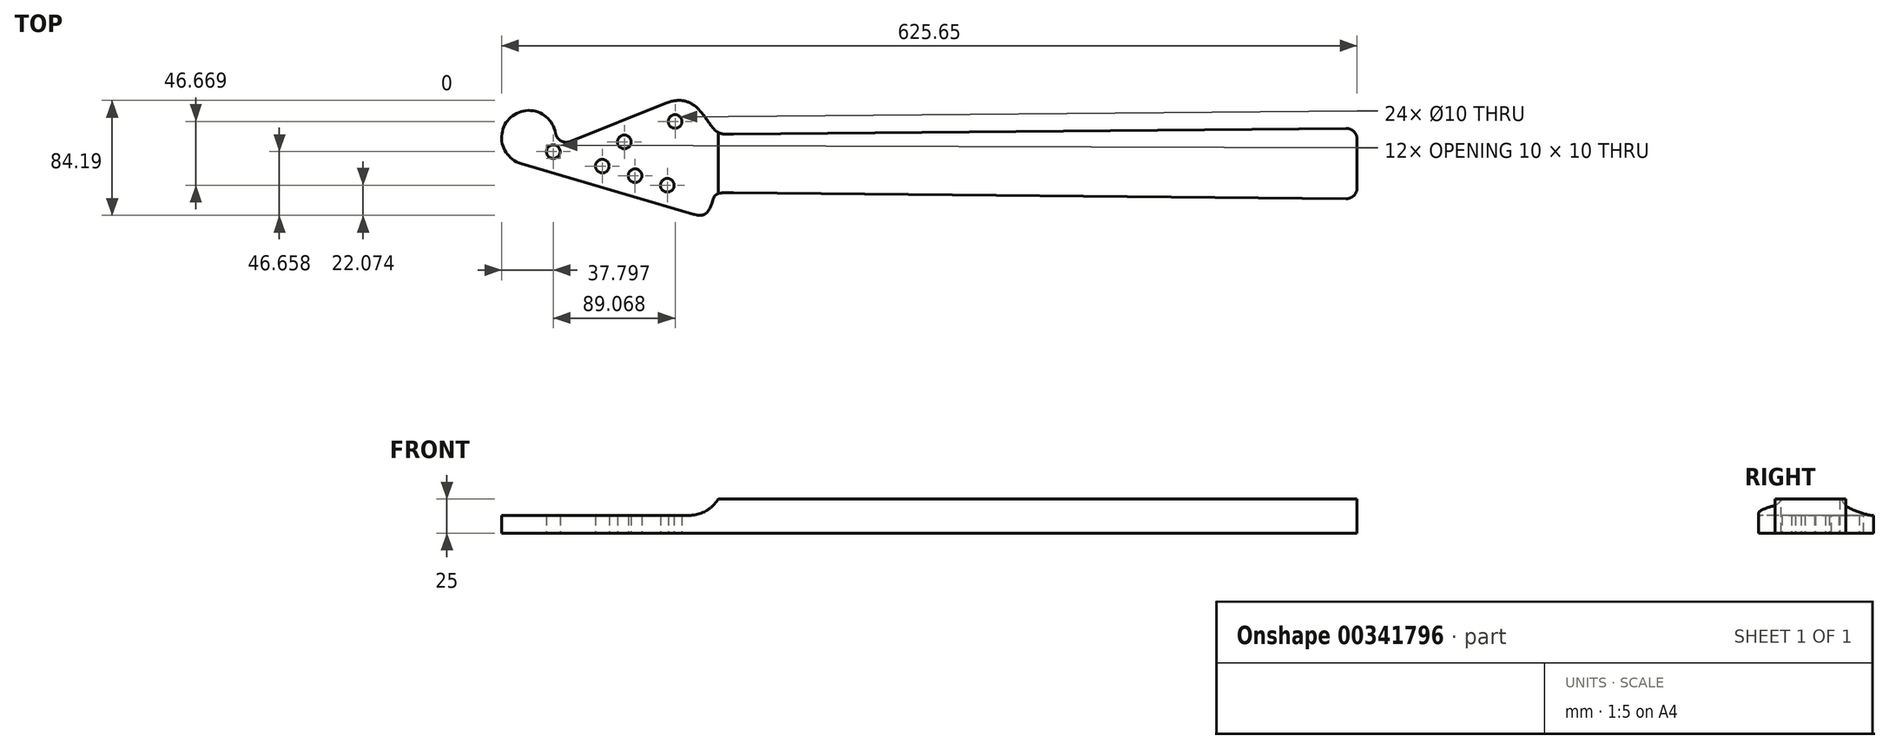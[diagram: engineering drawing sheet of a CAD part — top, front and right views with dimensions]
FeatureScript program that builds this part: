
annotation { "Feature Type Name" : "Feature", "Feature Type Description" : "" }
export const myFeature = defineFeature(function(context is Context, id is Id, definition is map)
    precondition{}
    {
        {
            var Q0;
            Q0=qCreatedBy(makeId("Top.planeOp"),FACE);
            var sketch = newSketch(context, id + "F0", { "sketchPlane" : qUnion([Q0])});
            skLineSegment(sketch, "E0", {"start": v(-545.56, 0) * mm, "end": v(270.45, 0) * mm, "construction": true});
            skLineSegment(sketch, "E1", {"start": v(-514.65, 21.5) * mm, "end": v(-514.65, -21.5) * mm, "construction": true});
            skText(sketch, "E2", { "text": "Nut", "fontName": "OpenSans-Regular.ttf"});
            skLineSegment(sketch, "E3", {"start": v(120.35, 27.5) * mm, "end": v(120.35, -27.5) * mm, "construction": true});
            skText(sketch, "E4", { "text": "Bridge\n", "fontName": "OpenSans-Regular.ttf"});
            skLineSegment(sketch, "E5", {"start": v(-514.65, 21.5) * mm, "end": v(120.35, 27.5) * mm, "construction": true});
            skLineSegment(sketch, "E6", {"start": v(-514.65, -21.5) * mm, "end": v(120.35, -27.5) * mm, "construction": true});
            skLineSegment(sketch, "E7", {"start": v(-514.65, 0) * mm, "end": v(120.35, 0) * mm});
            const initialGuessF0  = {"E2": [-0.53875, 0.11756, 1, 0, 0.01067], "E4": [0.1311, 0.11455, 1, 0, 0.02259]};
            skSetInitialGuess(sketch, initialGuessF0);
            skSolve(sketch);
        }
        {
            var Q0;
            Q0=qCreatedBy(makeId("Top.planeOp"),FACE);
            var sketch = newSketch(context, id + "F1", { "sketchPlane" : qUnion([Q0])});
            skLineSegment(sketch, "E8", {"start": v(-514.65, 21.5) * mm, "end": v(-514.65, -21.5) * mm});
            skSolve(sketch);
        }
        {
            var Q0;
            Q0=qCreatedBy(makeId("Top.planeOp"),FACE);
            var sketch = newSketch(context, id + "F2", { "sketchPlane" : qUnion([Q0])});
            skLineSegment(sketch, "E9", {"start": v(-479, 35.64) * mm, "end": v(-479, 0) * mm});
            skLineSegment(sketch, "E10", {"start": v(-514.65, 37.76) * mm, "end": v(120.35, 0) * mm, "construction": true});
            skLineSegment(sketch, "E11", {"start": v(120.35, 0) * mm, "end": v(-514.65, -21.5) * mm, "construction": true});
            skLineSegment(sketch, "E12", {"start": v(-514.65, 0) * mm, "end": v(-514.65, 37.76) * mm});
            skLineSegment(sketch, "E13", {"start": v(-514.65, 0) * mm, "end": v(-479, 0) * mm});
            skLineSegment(sketch, "E14", {"start": v(-445.37, 33.64) * mm, "end": v(-445.37, 0) * mm});
            skLineSegment(sketch, "E15", {"start": v(-445.37, 0) * mm, "end": v(-479, 0) * mm});
            skLineSegment(sketch, "E16", {"start": v(-445.37, 0) * mm, "end": v(-413.62, 0) * mm});
            skLineSegment(sketch, "E17", {"start": v(-413.62, 0) * mm, "end": v(-413.62, 31.75) * mm});
            skLineSegment(sketch, "E18", {"start": v(-413.62, 0) * mm, "end": v(-383.65, 0) * mm});
            skLineSegment(sketch, "E19", {"start": v(-383.65, 0) * mm, "end": v(-383.65, 29.97) * mm});
            skLineSegment(sketch, "E20", {"start": v(-383.65, 0) * mm, "end": v(-355.36, 0) * mm});
            skLineSegment(sketch, "E21", {"start": v(-355.36, 0) * mm, "end": v(-355.36, 28.29) * mm});
            skLineSegment(sketch, "E22", {"start": v(-355.36, 0) * mm, "end": v(-328.66, 0) * mm});
            skLineSegment(sketch, "E23", {"start": v(-328.66, 0) * mm, "end": v(-328.66, 26.7) * mm});
            skLineSegment(sketch, "E24", {"start": v(-328.66, 0) * mm, "end": v(-303.46, 0) * mm});
            skLineSegment(sketch, "E25", {"start": v(-303.46, 0) * mm, "end": v(-303.46, 25.2) * mm});
            skLineSegment(sketch, "E26", {"start": v(-303.46, 0) * mm, "end": v(-279.67, 0) * mm});
            skLineSegment(sketch, "E27", {"start": v(-279.67, 0) * mm, "end": v(-279.67, 23.79) * mm});
            skLineSegment(sketch, "E28", {"start": v(-279.67, 0) * mm, "end": v(-257.22, 0) * mm});
            skLineSegment(sketch, "E29", {"start": v(-257.22, 0) * mm, "end": v(-257.22, 22.45) * mm});
            skLineSegment(sketch, "E30", {"start": v(-257.22, 0) * mm, "end": v(-236.03, 0) * mm});
            skLineSegment(sketch, "E31", {"start": v(-236.03, 0) * mm, "end": v(-236.03, 21.2) * mm});
            skLineSegment(sketch, "E32", {"start": v(-236.03, 0) * mm, "end": v(-216.03, 0) * mm});
            skPoint(sketch, "E32.endSnap0", {"position": v(-246.63, 0) * mm});
            skLineSegment(sketch, "E33", {"start": v(-216.03, 0) * mm, "end": v(-216.03, 20) * mm});
            skLineSegment(sketch, "E34", {"start": v(-216.03, 0) * mm, "end": v(-197.15, 0) * mm});
            skLineSegment(sketch, "E35", {"start": v(-197.15, 0) * mm, "end": v(-197.15, 18.88) * mm});
            skLineSegment(sketch, "E36", {"start": v(-197.15, 0) * mm, "end": v(-179.33, 0) * mm});
            skLineSegment(sketch, "E37", {"start": v(-179.33, 0) * mm, "end": v(-179.33, 17.82) * mm});
            skLineSegment(sketch, "E38", {"start": v(-179.33, 0) * mm, "end": v(-162.5, 0) * mm});
            skLineSegment(sketch, "E39", {"start": v(-162.5, 0) * mm, "end": v(-162.5, 16.82) * mm});
            skLineSegment(sketch, "E40", {"start": v(-162.5, 0) * mm, "end": v(-146.63, 0) * mm});
            skLineSegment(sketch, "E41", {"start": v(-146.63, 0) * mm, "end": v(-146.63, 15.88) * mm});
            skLineSegment(sketch, "E42", {"start": v(-146.63, 0) * mm, "end": v(-131.65, 0) * mm});
            skLineSegment(sketch, "E43", {"start": v(-131.65, 0) * mm, "end": v(-131.65, 14.98) * mm});
            skLineSegment(sketch, "E44", {"start": v(-131.65, 0) * mm, "end": v(-117.5, 0) * mm});
            skLineSegment(sketch, "E45", {"start": v(-117.5, 0) * mm, "end": v(-117.5, 14.14) * mm});
            skLineSegment(sketch, "E46", {"start": v(-117.5, 0) * mm, "end": v(-104.16, 0) * mm});
            skLineSegment(sketch, "E47", {"start": v(-104.16, 0) * mm, "end": v(-104.16, 13.35) * mm});
            skLineSegment(sketch, "E48", {"start": v(-104.16, 0) * mm, "end": v(-91.56, 0) * mm});
            skLineSegment(sketch, "E49", {"start": v(-91.56, 0) * mm, "end": v(-91.56, 12.6) * mm});
            skLineSegment(sketch, "E50", {"start": v(-91.56, 0) * mm, "end": v(-79.66, 0) * mm});
            skLineSegment(sketch, "E51", {"start": v(-79.66, 0) * mm, "end": v(-79.66, 11.9) * mm});
            skLineSegment(sketch, "E52", {"start": v(-79.66, 0) * mm, "end": v(-68.44, 0) * mm});
            skLineSegment(sketch, "E53", {"start": v(-68.44, 0) * mm, "end": v(-68.44, 11.23) * mm});
            skSolve(sketch);
        }
        {
            var Q0;
            Q0=qCreatedBy(makeId("Top.planeOp"),FACE);
            var sketch = newSketch(context, id + "F3", { "sketchPlane" : qUnion([Q0])});
            skLineSegment(sketch, "E54", {"start": v(-514.65, 21.5) * mm, "end": v(-514.65, -21.5) * mm});
            skLineSegment(sketch, "E55", {"start": v(-514.65, -21.5) * mm, "end": v(-66.51, -25.73) * mm});
            skLineSegment(sketch, "E56", {"start": v(-58.44, -17.73) * mm, "end": v(-58.44, 17.73) * mm});
            skLineSegment(sketch, "E57", {"start": v(-66.51, 25.73) * mm, "end": v(-514.65, 21.5) * mm});
            skLineSegment(sketch, "E58", {"start": v(-68.44, 0) * mm, "end": v(-58.44, 0) * mm});
            skPoint(sketch, "E59.visualSharp", {"position": v(-58.44, -25.81) * mm});
            skArc(sketch, "E59.filletArc", {"start": v(-66.51, -25.73) * mm, "mid": v(-60.8, -23.42) * mm, "end": v(-58.44, -17.73) * mm});
            skPoint(sketch, "E60.visualSharp", {"position": v(-58.44, 25.81) * mm});
            skArc(sketch, "E60.filletArc", {"start": v(-58.44, 17.73) * mm, "mid": v(-60.8, 23.42) * mm, "end": v(-66.51, 25.73) * mm});
            skSolve(sketch);
        }
        {
            var Q0;
            Q0=qSketchRegion(id+"F3",true);
            extrude(context, id + "F4", {"entities" : qUnion([Q0]), "depth" : 6 * mm});
        }
        {
            var Q0;
            Q0=makeQuery(id+"F4.opExtrude","CAP_FACE",FACE,{"disambiguationData":[OSD([sQuery(id+"F3.wireOp",EDGE,"E54"),sQuery(id+"F3.wireOp",EDGE,"E55"),sQuery(id+"F3.wireOp",EDGE,"E56"),sQuery(id+"F3.wireOp",EDGE,"E57")])],"isStart":false});
            cPlane(context, id + "F5", {"entities" : qUnion([Q0]), "cplaneType" : CPlaneType.OFFSET, "offset" : 0 * mm, "width" : 150 * mm, "height" : 150 * mm});
        }
        {
            var Q0;
            Q0=qCreatedBy(id+"F5.planeOp",FACE);
            var sketch = newSketch(context, id + "F6", { "sketchPlane" : qUnion([Q0])});
            skCircle(sketch, "E61", {"center": v(-429.5, 0) * mm, "radius": 3 * mm});
            skCircle(sketch, "E62", {"center": v(-369.5, 0) * mm, "radius": 3 * mm});
            skCircle(sketch, "E63", {"center": v(-316.06, 0) * mm, "radius": 3 * mm});
            skCircle(sketch, "E64", {"center": v(-268.45, 0) * mm, "radius": 3 * mm});
            skCircle(sketch, "E65", {"center": v(-226.03, 12.11) * mm, "radius": 3 * mm});
            skCircle(sketch, "E66", {"center": v(-226.03, -12.11) * mm, "radius": 3 * mm});
            skLineSegment(sketch, "E67", {"start": v(-226.03, 0) * mm, "end": v(-226.03, 12.11) * mm, "construction": true});
            skCircle(sketch, "E68", {"center": v(-170.92, 0) * mm, "radius": 3 * mm});
            skCircle(sketch, "E69", {"center": v(-139.14, 0) * mm, "radius": 3 * mm});
            skCircle(sketch, "E70", {"center": v(-110.83, 0) * mm, "radius": 3 * mm});
            skCircle(sketch, "E71", {"center": v(-85.6, 0) * mm, "radius": 3 * mm});
            skLineSegment(sketch, "E72.0", {"start": v(-514.65, 21.5) * mm, "end": v(120.35, 27.5) * mm});
            skLineSegment(sketch, "E73", {"start": v(-226.03, 0) * mm, "end": v(-226.03, 24.23) * mm, "construction": true});
            skSolve(sketch);
        }
        {
            var Q0;
            Q0=qSketchRegion(id+"F6",true);
            var Q1;
            Q1=makeQuery(id+"F4.opExtrude","CAP_FACE",FACE,{"disambiguationData":[OSD([sQuery(id+"F3.wireOp",EDGE,"E54"),sQuery(id+"F3.wireOp",EDGE,"E55"),sQuery(id+"F3.wireOp",EDGE,"E56"),sQuery(id+"F3.wireOp",EDGE,"E57")])],"isStart":true});
            extrude(context, id + "F7", {"entities" : qUnion([Q0]), "operationType" : NewBodyOperationType.REMOVE, "oppositeDirection" : true, "endBoundEntityFace" : qUnion([Q1]), "depth" : 2 * mm});
        }
        {
            var Q0;
            Q0=makeQuery(id+"F4.opExtrude","SWEPT_FACE",FACE,{"disambiguationData":[OSD([sQuery(id+"F3.wireOp",EDGE,"E56")])]});
            var sketch = newSketch(context, id + "F8", { "sketchPlane" : qUnion([Q0])});
            skArc(sketch, "E74", {"start": v(53.48, 0) * mm, "mid": v(0, 6) * mm, "end": v(-53.48, 0) * mm});
            skLineSegment(sketch, "E75", {"start": v(-53.48, 0) * mm, "end": v(-53.48, 6) * mm});
            skLineSegment(sketch, "E76", {"start": v(-53.48, 6) * mm, "end": v(53.48, 6) * mm});
            skLineSegment(sketch, "E77", {"start": v(53.48, 6) * mm, "end": v(53.48, 0) * mm});
            skSolve(sketch);
        }
        {
            var Q0;
            Q0=qSketchRegion(id+"F8",true);
            extrude(context, id + "F9", {"entities" : qUnion([Q0]), "operationType" : NewBodyOperationType.REMOVE, "endBound" : BoundingType.THROUGH_ALL, "oppositeDirection" : true, "depth" : 25 * mm});
        }
        {
            var Q0;
            Q0=qCreatedBy(id+"F5.planeOp",FACE);
            var sketch = newSketch(context, id + "F10", { "sketchPlane" : qUnion([Q0])});
            skLineSegment(sketch, "E78.0", {"start": v(-514.65, 21.5) * mm, "end": v(-514.65, -21.5) * mm});
            skLineSegment(sketch, "E79.0", {"start": v(-58.44, 25.76) * mm, "end": v(-58.44, -25.76) * mm});
            skLineSegment(sketch, "E80", {"start": v(-514.65, 18.5) * mm, "end": v(-58.44, 22.81) * mm, "construction": true});
            skLineSegment(sketch, "E81", {"start": v(-514.65, -18.5) * mm, "end": v(-58.44, -22.81) * mm, "construction": true});
            skLineSegment(sketch, "E82", {"start": v(-479, 18.84) * mm, "end": v(-479, -18.84) * mm});
            skLineSegment(sketch, "E83", {"start": v(-445.37, 19.15) * mm, "end": v(-445.37, -19.15) * mm});
            skArc(sketch, "E84.0.startCap", {"start": v(-479.3, 18.84) * mm, "mid": v(-479, 19.14) * mm, "end": v(-478.7, 18.84) * mm});
            skArc(sketch, "E84.0.endCap", {"start": v(-478.7, -18.84) * mm, "mid": v(-479, -19.14) * mm, "end": v(-479.3, -18.84) * mm});
            skLineSegment(sketch, "E84.0.left", {"start": v(-478.7, 18.84) * mm, "end": v(-478.7, -18.84) * mm});
            skLineSegment(sketch, "E84.0.right", {"start": v(-479.3, 18.84) * mm, "end": v(-479.3, -18.84) * mm});
            skArc(sketch, "E85.0.startCap", {"start": v(-445.67, 19.15) * mm, "mid": v(-445.37, 19.45) * mm, "end": v(-445.07, 19.15) * mm});
            skArc(sketch, "E85.0.endCap", {"start": v(-445.07, -19.15) * mm, "mid": v(-445.37, -19.45) * mm, "end": v(-445.67, -19.15) * mm});
            skLineSegment(sketch, "E85.0.left", {"start": v(-445.07, 19.15) * mm, "end": v(-445.07, -19.15) * mm});
            skLineSegment(sketch, "E85.0.right", {"start": v(-445.67, 19.15) * mm, "end": v(-445.67, -19.15) * mm});
            skLineSegment(sketch, "E86", {"start": v(-413.62, 19.45) * mm, "end": v(-413.62, -19.45) * mm});
            skLineSegment(sketch, "E87", {"start": v(-383.65, 19.74) * mm, "end": v(-383.65, -19.74) * mm});
            skArc(sketch, "E88.0.startCap", {"start": v(-413.92, 19.45) * mm, "mid": v(-413.62, 19.75) * mm, "end": v(-413.32, 19.45) * mm});
            skArc(sketch, "E88.0.endCap", {"start": v(-413.32, -19.45) * mm, "mid": v(-413.62, -19.75) * mm, "end": v(-413.92, -19.45) * mm});
            skLineSegment(sketch, "E88.0.left", {"start": v(-413.32, 19.45) * mm, "end": v(-413.32, -19.45) * mm});
            skLineSegment(sketch, "E88.0.right", {"start": v(-413.92, 19.45) * mm, "end": v(-413.92, -19.45) * mm});
            skArc(sketch, "E89.0.startCap", {"start": v(-383.95, 19.74) * mm, "mid": v(-383.65, 20.04) * mm, "end": v(-383.35, 19.74) * mm});
            skArc(sketch, "E89.0.endCap", {"start": v(-383.35, -19.74) * mm, "mid": v(-383.65, -20.04) * mm, "end": v(-383.95, -19.74) * mm});
            skLineSegment(sketch, "E89.0.left", {"start": v(-383.35, 19.74) * mm, "end": v(-383.35, -19.74) * mm});
            skLineSegment(sketch, "E89.0.right", {"start": v(-383.95, 19.74) * mm, "end": v(-383.95, -19.74) * mm});
            skLineSegment(sketch, "E90", {"start": v(-355.36, -20) * mm, "end": v(-355.36, 20) * mm});
            skArc(sketch, "E91.0.startCap", {"start": v(-355.06, -20) * mm, "mid": v(-355.36, -20.3) * mm, "end": v(-355.66, -20) * mm});
            skArc(sketch, "E91.0.endCap", {"start": v(-355.66, 20) * mm, "mid": v(-355.36, 20.3) * mm, "end": v(-355.06, 20) * mm});
            skLineSegment(sketch, "E91.0.left", {"start": v(-355.66, -20) * mm, "end": v(-355.66, 20) * mm});
            skLineSegment(sketch, "E91.0.right", {"start": v(-355.06, -20) * mm, "end": v(-355.06, 20) * mm});
            skLineSegment(sketch, "E92", {"start": v(-328.66, -20.26) * mm, "end": v(-328.66, 20.26) * mm});
            skArc(sketch, "E93.0.startCap", {"start": v(-328.36, -20.26) * mm, "mid": v(-328.66, -20.56) * mm, "end": v(-328.96, -20.26) * mm});
            skArc(sketch, "E93.0.endCap", {"start": v(-328.96, 20.26) * mm, "mid": v(-328.66, 20.56) * mm, "end": v(-328.36, 20.26) * mm});
            skLineSegment(sketch, "E93.0.left", {"start": v(-328.96, -20.26) * mm, "end": v(-328.96, 20.26) * mm});
            skLineSegment(sketch, "E93.0.right", {"start": v(-328.36, -20.26) * mm, "end": v(-328.36, 20.26) * mm});
            skLineSegment(sketch, "E94", {"start": v(-303.46, 20.5) * mm, "end": v(-303.46, -20.5) * mm});
            skArc(sketch, "E95.0.startCap", {"start": v(-303.76, 20.5) * mm, "mid": v(-303.46, 20.8) * mm, "end": v(-303.16, 20.5) * mm});
            skArc(sketch, "E95.0.endCap", {"start": v(-303.16, -20.5) * mm, "mid": v(-303.46, -20.8) * mm, "end": v(-303.76, -20.5) * mm});
            skLineSegment(sketch, "E95.0.left", {"start": v(-303.16, 20.5) * mm, "end": v(-303.16, -20.5) * mm});
            skLineSegment(sketch, "E95.0.right", {"start": v(-303.76, 20.5) * mm, "end": v(-303.76, -20.5) * mm});
            skLineSegment(sketch, "E96", {"start": v(-279.67, 20.72) * mm, "end": v(-279.67, -20.72) * mm});
            skArc(sketch, "E97.0.startCap", {"start": v(-279.97, 20.72) * mm, "mid": v(-279.67, 21.02) * mm, "end": v(-279.37, 20.72) * mm});
            skArc(sketch, "E97.0.endCap", {"start": v(-279.37, -20.72) * mm, "mid": v(-279.67, -21.02) * mm, "end": v(-279.97, -20.72) * mm});
            skLineSegment(sketch, "E97.0.left", {"start": v(-279.37, 20.72) * mm, "end": v(-279.37, -20.72) * mm});
            skLineSegment(sketch, "E97.0.right", {"start": v(-279.97, 20.72) * mm, "end": v(-279.97, -20.72) * mm});
            skLineSegment(sketch, "E98", {"start": v(-257.22, -20.93) * mm, "end": v(-257.22, 20.93) * mm});
            skArc(sketch, "E99.0.startCap", {"start": v(-256.92, -20.93) * mm, "mid": v(-257.22, -21.23) * mm, "end": v(-257.52, -20.93) * mm});
            skArc(sketch, "E99.0.endCap", {"start": v(-257.52, 20.93) * mm, "mid": v(-257.22, 21.23) * mm, "end": v(-256.92, 20.93) * mm});
            skLineSegment(sketch, "E99.0.left", {"start": v(-257.52, -20.93) * mm, "end": v(-257.52, 20.93) * mm});
            skLineSegment(sketch, "E99.0.right", {"start": v(-256.92, -20.93) * mm, "end": v(-256.92, 20.93) * mm});
            skLineSegment(sketch, "E100", {"start": v(-236.03, 21.13) * mm, "end": v(-236.03, -21.13) * mm});
            skArc(sketch, "E101.0.startCap", {"start": v(-236.33, 21.13) * mm, "mid": v(-236.03, 21.43) * mm, "end": v(-235.73, 21.13) * mm});
            skArc(sketch, "E101.0.endCap", {"start": v(-235.73, -21.13) * mm, "mid": v(-236.03, -21.43) * mm, "end": v(-236.33, -21.13) * mm});
            skLineSegment(sketch, "E101.0.left", {"start": v(-235.73, 21.13) * mm, "end": v(-235.73, -21.13) * mm});
            skLineSegment(sketch, "E101.0.right", {"start": v(-236.33, 21.13) * mm, "end": v(-236.33, -21.13) * mm});
            skLineSegment(sketch, "E102", {"start": v(-216.03, 21.32) * mm, "end": v(-216.03, -21.32) * mm});
            skArc(sketch, "E103.0.startCap", {"start": v(-216.33, 21.32) * mm, "mid": v(-216.03, 21.62) * mm, "end": v(-215.73, 21.32) * mm});
            skArc(sketch, "E103.0.endCap", {"start": v(-215.73, -21.32) * mm, "mid": v(-216.03, -21.62) * mm, "end": v(-216.33, -21.32) * mm});
            skLineSegment(sketch, "E103.0.left", {"start": v(-215.73, 21.32) * mm, "end": v(-215.73, -21.32) * mm});
            skLineSegment(sketch, "E103.0.right", {"start": v(-216.33, 21.32) * mm, "end": v(-216.33, -21.32) * mm});
            skLineSegment(sketch, "E104", {"start": v(-197.15, 21.5) * mm, "end": v(-197.15, -21.5) * mm});
            skArc(sketch, "E105.0.startCap", {"start": v(-197.45, 21.5) * mm, "mid": v(-197.15, 21.8) * mm, "end": v(-196.85, 21.5) * mm});
            skArc(sketch, "E105.0.endCap", {"start": v(-196.85, -21.5) * mm, "mid": v(-197.15, -21.8) * mm, "end": v(-197.45, -21.5) * mm});
            skLineSegment(sketch, "E105.0.left", {"start": v(-196.85, 21.5) * mm, "end": v(-196.85, -21.5) * mm});
            skLineSegment(sketch, "E105.0.right", {"start": v(-197.45, 21.5) * mm, "end": v(-197.45, -21.5) * mm});
            skLineSegment(sketch, "E106", {"start": v(-179.33, 21.67) * mm, "end": v(-179.33, -21.67) * mm});
            skArc(sketch, "E107.0.startCap", {"start": v(-179.63, 21.67) * mm, "mid": v(-179.33, 21.97) * mm, "end": v(-179.03, 21.67) * mm});
            skArc(sketch, "E107.0.endCap", {"start": v(-179.03, -21.67) * mm, "mid": v(-179.33, -21.97) * mm, "end": v(-179.63, -21.67) * mm});
            skLineSegment(sketch, "E107.0.left", {"start": v(-179.03, 21.67) * mm, "end": v(-179.03, -21.67) * mm});
            skLineSegment(sketch, "E107.0.right", {"start": v(-179.63, 21.67) * mm, "end": v(-179.63, -21.67) * mm});
            skLineSegment(sketch, "E108", {"start": v(-162.5, 21.83) * mm, "end": v(-162.5, -21.83) * mm});
            skArc(sketch, "E109.0.startCap", {"start": v(-162.8, 21.83) * mm, "mid": v(-162.5, 22.13) * mm, "end": v(-162.2, 21.83) * mm});
            skArc(sketch, "E109.0.endCap", {"start": v(-162.2, -21.83) * mm, "mid": v(-162.5, -22.13) * mm, "end": v(-162.8, -21.83) * mm});
            skLineSegment(sketch, "E109.0.left", {"start": v(-162.2, 21.83) * mm, "end": v(-162.2, -21.83) * mm});
            skLineSegment(sketch, "E109.0.right", {"start": v(-162.8, 21.83) * mm, "end": v(-162.8, -21.83) * mm});
            skLineSegment(sketch, "E110", {"start": v(-146.63, 21.98) * mm, "end": v(-146.63, -21.98) * mm});
            skArc(sketch, "E111.0.startCap", {"start": v(-146.93, 21.98) * mm, "mid": v(-146.63, 22.28) * mm, "end": v(-146.33, 21.98) * mm});
            skArc(sketch, "E111.0.endCap", {"start": v(-146.33, -21.98) * mm, "mid": v(-146.63, -22.28) * mm, "end": v(-146.93, -21.98) * mm});
            skLineSegment(sketch, "E111.0.left", {"start": v(-146.33, 21.98) * mm, "end": v(-146.33, -21.98) * mm});
            skLineSegment(sketch, "E111.0.right", {"start": v(-146.93, 21.98) * mm, "end": v(-146.93, -21.98) * mm});
            skLineSegment(sketch, "E112", {"start": v(-131.65, 22.12) * mm, "end": v(-131.65, -22.12) * mm});
            skArc(sketch, "E113.0.startCap", {"start": v(-131.95, 22.12) * mm, "mid": v(-131.65, 22.42) * mm, "end": v(-131.35, 22.12) * mm});
            skArc(sketch, "E113.0.endCap", {"start": v(-131.35, -22.12) * mm, "mid": v(-131.65, -22.42) * mm, "end": v(-131.95, -22.12) * mm});
            skLineSegment(sketch, "E113.0.left", {"start": v(-131.35, 22.12) * mm, "end": v(-131.35, -22.12) * mm});
            skLineSegment(sketch, "E113.0.right", {"start": v(-131.95, 22.12) * mm, "end": v(-131.95, -22.12) * mm});
            skLineSegment(sketch, "E114", {"start": v(-117.5, 22.25) * mm, "end": v(-117.5, -22.25) * mm});
            skArc(sketch, "E115.0.startCap", {"start": v(-117.8, 22.25) * mm, "mid": v(-117.5, 22.55) * mm, "end": v(-117.2, 22.25) * mm});
            skArc(sketch, "E115.0.endCap", {"start": v(-117.2, -22.25) * mm, "mid": v(-117.5, -22.55) * mm, "end": v(-117.8, -22.25) * mm});
            skLineSegment(sketch, "E115.0.left", {"start": v(-117.2, 22.25) * mm, "end": v(-117.2, -22.25) * mm});
            skLineSegment(sketch, "E115.0.right", {"start": v(-117.8, 22.25) * mm, "end": v(-117.8, -22.25) * mm});
            skLineSegment(sketch, "E116", {"start": v(-104.16, 22.38) * mm, "end": v(-104.16, -22.38) * mm});
            skArc(sketch, "E117.0.startCap", {"start": v(-104.46, 22.38) * mm, "mid": v(-104.16, 22.68) * mm, "end": v(-103.86, 22.38) * mm});
            skArc(sketch, "E117.0.endCap", {"start": v(-103.86, -22.38) * mm, "mid": v(-104.16, -22.68) * mm, "end": v(-104.46, -22.38) * mm});
            skLineSegment(sketch, "E117.0.left", {"start": v(-103.86, 22.38) * mm, "end": v(-103.86, -22.38) * mm});
            skLineSegment(sketch, "E117.0.right", {"start": v(-104.46, 22.38) * mm, "end": v(-104.46, -22.38) * mm});
            skLineSegment(sketch, "E118", {"start": v(-91.56, 22.5) * mm, "end": v(-91.56, -22.5) * mm});
            skArc(sketch, "E119.0.startCap", {"start": v(-91.86, 22.5) * mm, "mid": v(-91.56, 22.8) * mm, "end": v(-91.26, 22.5) * mm});
            skArc(sketch, "E119.0.endCap", {"start": v(-91.26, -22.5) * mm, "mid": v(-91.56, -22.8) * mm, "end": v(-91.86, -22.5) * mm});
            skLineSegment(sketch, "E119.0.left", {"start": v(-91.26, 22.5) * mm, "end": v(-91.26, -22.5) * mm});
            skLineSegment(sketch, "E119.0.right", {"start": v(-91.86, 22.5) * mm, "end": v(-91.86, -22.5) * mm});
            skLineSegment(sketch, "E120", {"start": v(-79.66, -22.61) * mm, "end": v(-79.66, 22.61) * mm});
            skArc(sketch, "E121.0.startCap", {"start": v(-79.36, -22.61) * mm, "mid": v(-79.66, -22.91) * mm, "end": v(-79.96, -22.61) * mm});
            skArc(sketch, "E121.0.endCap", {"start": v(-79.96, 22.61) * mm, "mid": v(-79.66, 22.91) * mm, "end": v(-79.36, 22.61) * mm});
            skLineSegment(sketch, "E121.0.left", {"start": v(-79.96, -22.61) * mm, "end": v(-79.96, 22.61) * mm});
            skLineSegment(sketch, "E121.0.right", {"start": v(-79.36, -22.61) * mm, "end": v(-79.36, 22.61) * mm});
            skLineSegment(sketch, "E122", {"start": v(-68.44, 22.72) * mm, "end": v(-68.44, -22.72) * mm});
            skArc(sketch, "E123.0.startCap", {"start": v(-68.74, 22.72) * mm, "mid": v(-68.44, 23.02) * mm, "end": v(-68.14, 22.72) * mm});
            skArc(sketch, "E123.0.endCap", {"start": v(-68.14, -22.72) * mm, "mid": v(-68.44, -23.02) * mm, "end": v(-68.74, -22.72) * mm});
            skLineSegment(sketch, "E123.0.left", {"start": v(-68.14, 22.72) * mm, "end": v(-68.14, -22.72) * mm});
            skLineSegment(sketch, "E123.0.right", {"start": v(-68.74, 22.72) * mm, "end": v(-68.74, -22.72) * mm});
            skSolve(sketch);
        }
        {
            var Q0;
            Q0=qSketchRegion(id+"F10",true);
            extrude(context, id + "F11", {"entities" : qUnion([Q0]), "operationType" : NewBodyOperationType.REMOVE, "oppositeDirection" : true, "depth" : 4 * mm});
        }
        {
            var Q0;
            Q0=makeQuery(id+"F4.opExtrude","SWEPT_FACE",FACE,{"disambiguationData":[OSD([sQuery(id+"F3.wireOp",EDGE,"E55")])]});
            var sketch = newSketch(context, id + "F12", { "sketchPlane" : qUnion([Q0])});
            skPoint(sketch, "E124.0", {"position": v(-429.48, 6) * mm});
            skLineSegment(sketch, "E125", {"start": v(-429.48, 6) * mm, "end": v(-429.48, 0) * mm, "construction": true});
            skCircle(sketch, "E126", {"center": v(-429.48, 2) * mm, "radius": 1 * mm});
            skLineSegment(sketch, "E127", {"start": v(-298.57, 2) * mm, "end": v(-514.42, 2) * mm, "construction": true});
            skPoint(sketch, "E128.0", {"position": v(-369.49, 6) * mm});
            skLineSegment(sketch, "E129", {"start": v(-369.49, 6) * mm, "end": v(-369.49, 0) * mm, "construction": true});
            skCircle(sketch, "E130", {"center": v(-369.49, 2) * mm, "radius": 1 * mm});
            skPoint(sketch, "E131.0", {"position": v(-316.05, 6) * mm});
            skPoint(sketch, "E132.0", {"position": v(-268.44, 6) * mm});
            skPoint(sketch, "E133.0", {"position": v(-225.9, 6) * mm});
            skPoint(sketch, "E134.0", {"position": v(-170.91, 6) * mm});
            skPoint(sketch, "E135.0", {"position": v(-139.14, 6) * mm});
            skPoint(sketch, "E136.0", {"position": v(-110.83, 6) * mm});
            skPoint(sketch, "E137.0", {"position": v(-85.6, 6) * mm});
            skLineSegment(sketch, "E138", {"start": v(-85.6, 6) * mm, "end": v(-85.6, 0) * mm, "construction": true});
            skLineSegment(sketch, "E139", {"start": v(-110.83, 6) * mm, "end": v(-110.83, 0) * mm, "construction": true});
            skLineSegment(sketch, "E140", {"start": v(-139.14, 6) * mm, "end": v(-139.14, 0) * mm, "construction": true});
            skLineSegment(sketch, "E141", {"start": v(-170.91, 6) * mm, "end": v(-170.91, 0) * mm, "construction": true});
            skLineSegment(sketch, "E142", {"start": v(-225.9, 6) * mm, "end": v(-225.9, 0) * mm, "construction": true});
            skLineSegment(sketch, "E143", {"start": v(-268.44, 6) * mm, "end": v(-268.44, 0) * mm, "construction": true});
            skLineSegment(sketch, "E144", {"start": v(-316.05, 6) * mm, "end": v(-316.05, 0) * mm, "construction": true});
            skCircle(sketch, "E145", {"center": v(-85.6, 2) * mm, "radius": 1 * mm});
            skCircle(sketch, "E146", {"center": v(-110.83, 2) * mm, "radius": 1 * mm});
            skCircle(sketch, "E147", {"center": v(-139.14, 2) * mm, "radius": 1 * mm});
            skCircle(sketch, "E148", {"center": v(-268.44, 2) * mm, "radius": 1 * mm});
            skLineSegment(sketch, "E149.0", {"start": v(-236.02, 0) * mm, "end": v(-236.22, 0) * mm});
            skLineSegment(sketch, "E150.0", {"start": v(-216.02, 0) * mm, "end": v(-216.2, 0) * mm});
            skPoint(sketch, "E151", {"position": v(-225.9, 2) * mm});
            skCircle(sketch, "E152", {"center": v(-316.05, 2) * mm, "radius": 1 * mm});
            skLineSegment(sketch, "E153", {"start": v(-216.02, 0) * mm, "end": v(-216.02, 4.13) * mm});
            skPoint(sketch, "E154", {"position": v(-216.02, 2) * mm});
            skCircle(sketch, "E155", {"center": v(-220.96, 2) * mm, "radius": 1 * mm});
            skCircle(sketch, "E156", {"center": v(-170.91, 2) * mm, "radius": 1 * mm});
            skCircle(sketch, "E157", {"center": v(-230.85, 2) * mm, "radius": 1 * mm});
            skSolve(sketch);
        }
        {
            var Q0;
            Q0=qSketchRegion(id+"F12",true);
            extrude(context, id + "F13", {"entities" : qUnion([Q0]), "operationType" : NewBodyOperationType.REMOVE, "oppositeDirection" : true, "depth" : 2 * mm});
        }
        {
            var Q0;
            Q0=qCreatedBy(makeId("Top.planeOp"),FACE);
            var sketch = newSketch(context, id + "F14", { "sketchPlane" : qUnion([Q0])});
            skLineSegment(sketch, "E158", {"start": v(-58.44, 70.43) * mm, "end": v(-58.44, -45.52) * mm});
            skLineSegment(sketch, "E159", {"start": v(-58.44, -45.52) * mm, "end": v(-731.05, -45.52) * mm});
            skLineSegment(sketch, "E160", {"start": v(-731.05, -45.52) * mm, "end": v(-731.05, 70.43) * mm});
            skLineSegment(sketch, "E161", {"start": v(-731.05, 70.43) * mm, "end": v(-58.44, 70.43) * mm});
            skSolve(sketch);
        }
        {
            var Q0;
            Q0=makeQuery(id+"F14.imprint","IMPRINT",FACE,{"disambiguationData":[TD([[makeQuery(id+"F14.imprint","IMPRINT",EDGE,{"derivedFrom":sQuery(id+"F14.wireOp",EDGE,"E158")}),-1.0]])]});
            extrude(context, id + "F15", {"entities" : qUnion([Q0]), "oppositeDirection" : true, "depth" : 25 * mm});
        }
        {
            var Q0;
            Q0=makeQuery(id+"F15.opExtrude","CAP_FACE",FACE,{"disambiguationData":[OSD([sQuery(id+"F14.wireOp",EDGE,"E158"),sQuery(id+"F14.wireOp",EDGE,"E159"),sQuery(id+"F14.wireOp",EDGE,"E160"),sQuery(id+"F14.wireOp",EDGE,"E161")])],"isStart":false});
            var sketch = newSketch(context, id + "F16", { "sketchPlane" : qUnion([Q0])});
            skLineSegment(sketch, "E162", {"start": v(-646.3, -8.69) * mm, "end": v(-562.92, 15.9) * mm, "construction": true});
            skLineSegment(sketch, "E163", {"start": v(-594.35, -15.84) * mm, "end": v(-557.22, -30.77) * mm, "construction": true});
            skCircle(sketch, "E164", {"center": v(-646.3, -8.69) * mm, "radius": 5 * mm});
            skCircle(sketch, "E165", {"center": v(-610.48, 1.87) * mm, "radius": 5 * mm});
            skCircle(sketch, "E166", {"center": v(-586.49, 8.95) * mm, "radius": 5 * mm});
            skCircle(sketch, "E167", {"center": v(-562.92, 15.9) * mm, "radius": 5 * mm});
            skCircle(sketch, "E168", {"center": v(-594.35, -15.84) * mm, "radius": 5 * mm});
            skCircle(sketch, "E169", {"center": v(-557.22, -30.77) * mm, "radius": 5 * mm});
            skSolve(sketch);
        }
        {
            var Q0;
            Q0=qSketchRegion(id+"F16",true);
            extrude(context, id + "F17", {"entities" : qUnion([Q0]), "operationType" : NewBodyOperationType.REMOVE, "endBound" : BoundingType.THROUGH_ALL, "oppositeDirection" : true, "depth" : 25 * mm});
        }
        {
            var Q0;
            Q0=qCreatedBy(makeId("Top.planeOp"),FACE);
            var sketch = newSketch(context, id + "F18", { "sketchPlane" : qUnion([Q0])});
            skLineSegment(sketch, "E170.0", {"start": v(-58.44, -17.73) * mm, "end": v(-58.44, 17.73) * mm});
            skLineSegment(sketch, "E171.0", {"start": v(-66.51, 25.73) * mm, "end": v(-514.65, 21.5) * mm});
            skLineSegment(sketch, "E172", {"start": v(-514.65, -21.5) * mm, "end": v(-66.51, -25.73) * mm});
            skFitSpline(sketch, "E173", {"points": [v(-514.65, -21.5) * mm, v(-528.95, -25.07) * mm, v(-543.18, -37.36) * mm], "startDerivative": vector(-60.43, 0.57) * mm, "endDerivative": vector(-63.56, 18.74) * mm});
            skLineSegment(sketch, "E174", {"start": v(-543.18, -37.36) * mm, "end": v(-669.86, 0) * mm});
            skArc(sketch, "E175", {"start": v(-644.68, 22.26) * mm, "mid": v(-677.39, 33.89) * mm, "end": v(-669.86, 0) * mm});
            skArc(sketch, "E176", {"start": v(-644.68, 22.26) * mm, "mid": v(-640.71, 16.59) * mm, "end": v(-633.8, 16.14) * mm});
            skLineSegment(sketch, "E177", {"start": v(-633.8, 16.14) * mm, "end": v(-564.31, 44.1) * mm});
            skFitSpline(sketch, "E178", {"points": [v(-514.65, 21.5) * mm, v(-528.8, 25.14) * mm, v(-564.31, 44.1) * mm], "startDerivative": vector(-47.75, -0.45) * mm, "endDerivative": vector(-104.5, -42.03) * mm});
            skPoint(sketch, "E179.visualSharp", {"position": v(-58.44, 25.81) * mm});
            skArc(sketch, "E179.filletArc", {"start": v(-58.44, 17.73) * mm, "mid": v(-60.8, 23.42) * mm, "end": v(-66.51, 25.73) * mm});
            skPoint(sketch, "E180.visualSharp", {"position": v(-58.44, -25.81) * mm});
            skArc(sketch, "E180.filletArc", {"start": v(-66.51, -25.73) * mm, "mid": v(-60.8, -23.42) * mm, "end": v(-58.44, -17.73) * mm});
            skLineSegment(sketch, "E181.0", {"start": v(-594.35, 15.84) * mm, "end": v(-557.22, 30.77) * mm});
            skLineSegment(sketch, "E182.0", {"start": v(-646.3, 8.69) * mm, "end": v(-562.92, -15.9) * mm});
            skSolve(sketch);
        }
        {
            var Q0;
            Q0=qSketchRegion(id+"F18",true);
            var Q1;
            Q1=qSketchRegion(id+"F16",true);
            extrude(context, id + "F19", {"entities" : qUnion([Q0, Q1]), "operationType" : NewBodyOperationType.INTERSECT, "oppositeDirection" : true, "depth" : 25 * mm});
        }
        {
            var Q0;
            Q0=qCreatedBy(makeId("Front.planeOp"),FACE);
            var sketch = newSketch(context, id + "F20", { "sketchPlane" : qUnion([Q0])});
            skFitSpline(sketch, "E183.0", {"points": [v(-890.47, -43.26) * mm, v(-896.1, -43.26) * mm, v(-905.56, -43.26) * mm, v(-915.53, -43.26) * mm, v(-922.39, -43.26) * mm, v(-926.45, -43.26) * mm, v(-929.27, -43.26) * mm, v(-931.32, -43.26) * mm, v(-933.43, -43.26) * mm, v(-935.75, -43.26) * mm, v(-938.24, -43.26) * mm, v(-941.76, -43.26) * mm, v(-946.45, -43.26) * mm, v(-951.34, -43.26) * mm, v(-955.27, -43.26) * mm, v(-958.2, -43.26) * mm, v(-961.08, -43.26) * mm, v(-964.99, -43.26) * mm, v(-970.12, -43.26) * mm, v(-977.21, -43.26) * mm, v(-984.33, -43.26) * mm, v(-991, -43.26) * mm, v(-996.58, -43.26) * mm, v(-1002.76, -43.26) * mm, v(-1009.65, -43.26) * mm, v(-1017.15, -43.26) * mm, v(-1027.88, -43.26) * mm, v(-1042.46, -43.26) * mm, v(-1061.2, -43.26) * mm, v(-1087.01, -43.26) * mm, v(-1112.84, -43.26) * mm, v(-1136.2, -43.26) * mm, v(-1151.88, -43.26) * mm, v(-1165.08, -43.26) * mm, v(-1173.51, -43.26) * mm, v(-1178.4, -43.26) * mm, v(-1181.05, -43.26) * mm, v(-1182.65, -43.26) * mm, v(-1183.5, -43.26) * mm, v(-1182.33, -43.26) * mm, v(-1177.99, -43.26) * mm, v(-1171.32, -43.26) * mm, v(-1162.96, -43.26) * mm, v(-1155.1, -43.26) * mm, v(-1148.57, -43.26) * mm, v(-1143.63, -43.26) * mm, v(-1138.74, -43.26) * mm, v(-1133.95, -43.26) * mm, v(-1129.25, -43.26) * mm, v(-1123.1, -43.26) * mm, v(-1115.6, -43.26) * mm, v(-1103.94, -43.26) * mm, v(-1092.64, -43.26) * mm, v(-1081.48, -43.26) * mm, v(-1073.11, -43.26) * mm, v(-1064.64, -43.26) * mm, v(-1055.9, -43.26) * mm, v(-1046.79, -43.26) * mm, v(-1037.14, -43.26) * mm, v(-1028.55, -43.26) * mm, v(-1021.28, -43.26) * mm, v(-1015.6, -43.26) * mm, v(-1009.73, -43.26) * mm, v(-1001.71, -43.26) * mm, v(-991.47, -43.26) * mm, v(-979.23, -43.26) * mm, v(-967.42, -43.26) * mm, v(-956.46, -43.26) * mm, v(-948.37, -43.26) * mm, v(-942.71, -43.26) * mm, v(-938.93, -43.26) * mm, v(-935.67, -43.26) * mm, v(-932.92, -43.26) * mm, v(-930.58, -43.26) * mm, v(-927.9, -43.26) * mm, v(-925.15, -43.26) * mm, v(-922.18, -43.26) * mm, v(-918.84, -43.26) * mm, v(-914.55, -43.26) * mm, v(-906.9, -43.26) * mm, v(-898.23, -43.26) * mm, v(-890.47, -43.26) * mm, v(-890.47, -43.26) * mm]});
            skFitSpline(sketch, "E184.0", {"points": [v(-890.47, -43.26) * mm, v(-896.1, -43.26) * mm, v(-905.56, -43.26) * mm, v(-915.53, -43.26) * mm, v(-922.39, -43.26) * mm, v(-926.45, -43.26) * mm, v(-929.27, -43.26) * mm, v(-931.32, -43.26) * mm, v(-933.43, -43.26) * mm, v(-935.75, -43.26) * mm, v(-938.24, -43.26) * mm, v(-941.76, -43.26) * mm, v(-946.45, -43.26) * mm, v(-951.34, -43.26) * mm, v(-955.27, -43.26) * mm, v(-958.2, -43.26) * mm, v(-961.08, -43.26) * mm, v(-964.99, -43.26) * mm, v(-970.12, -43.26) * mm, v(-977.21, -43.26) * mm, v(-984.33, -43.26) * mm, v(-991, -43.26) * mm, v(-996.58, -43.26) * mm, v(-1002.76, -43.26) * mm, v(-1009.65, -43.26) * mm, v(-1017.15, -43.26) * mm, v(-1027.88, -43.26) * mm, v(-1042.46, -43.26) * mm, v(-1061.2, -43.26) * mm, v(-1087.01, -43.26) * mm, v(-1112.84, -43.26) * mm, v(-1136.2, -43.26) * mm, v(-1151.88, -43.26) * mm, v(-1165.08, -43.26) * mm, v(-1173.51, -43.26) * mm, v(-1178.4, -43.26) * mm, v(-1181.05, -43.26) * mm, v(-1182.65, -43.26) * mm, v(-1183.5, -43.26) * mm, v(-1182.33, -43.26) * mm, v(-1177.99, -43.26) * mm, v(-1171.32, -43.26) * mm, v(-1162.96, -43.26) * mm, v(-1155.1, -43.26) * mm, v(-1148.57, -43.26) * mm, v(-1143.63, -43.26) * mm, v(-1138.74, -43.26) * mm, v(-1133.95, -43.26) * mm, v(-1129.25, -43.26) * mm, v(-1123.1, -43.26) * mm, v(-1115.6, -43.26) * mm, v(-1103.94, -43.26) * mm, v(-1092.64, -43.26) * mm, v(-1081.48, -43.26) * mm, v(-1073.11, -43.26) * mm, v(-1064.64, -43.26) * mm, v(-1055.9, -43.26) * mm, v(-1046.79, -43.26) * mm, v(-1037.14, -43.26) * mm, v(-1028.55, -43.26) * mm, v(-1021.28, -43.26) * mm, v(-1015.6, -43.26) * mm, v(-1009.73, -43.26) * mm, v(-1001.71, -43.26) * mm, v(-991.47, -43.26) * mm, v(-979.23, -43.26) * mm, v(-967.42, -43.26) * mm, v(-956.46, -43.26) * mm, v(-948.37, -43.26) * mm, v(-942.71, -43.26) * mm, v(-938.93, -43.26) * mm, v(-935.67, -43.26) * mm, v(-932.92, -43.26) * mm, v(-930.58, -43.26) * mm, v(-927.9, -43.26) * mm, v(-925.15, -43.26) * mm, v(-922.18, -43.26) * mm, v(-918.84, -43.26) * mm, v(-914.55, -43.26) * mm, v(-906.9, -43.26) * mm, v(-898.23, -43.26) * mm, v(-890.47, -43.26) * mm, v(-890.47, -43.26) * mm]});
            skLineSegment(sketch, "E185.0.0", {"start": v(-109.76, -43.26) * mm, "end": v(-109.76, -43.26) * mm});
            skFitSpline(sketch, "E185.0.1", {"points": [v(-890.47, -43.26) * mm, v(-896.1, -43.26) * mm, v(-905.56, -43.26) * mm, v(-915.53, -43.26) * mm, v(-922.39, -43.26) * mm, v(-926.45, -43.26) * mm, v(-929.27, -43.26) * mm, v(-931.32, -43.26) * mm, v(-933.43, -43.26) * mm, v(-935.75, -43.26) * mm, v(-938.24, -43.26) * mm, v(-941.76, -43.26) * mm, v(-946.45, -43.26) * mm, v(-951.34, -43.26) * mm, v(-955.27, -43.26) * mm, v(-958.2, -43.26) * mm, v(-961.08, -43.26) * mm, v(-964.99, -43.26) * mm, v(-970.12, -43.26) * mm, v(-977.21, -43.26) * mm, v(-984.33, -43.26) * mm, v(-991, -43.26) * mm, v(-996.58, -43.26) * mm, v(-1002.76, -43.26) * mm, v(-1009.65, -43.26) * mm, v(-1017.15, -43.26) * mm, v(-1027.88, -43.26) * mm, v(-1042.46, -43.26) * mm, v(-1061.2, -43.26) * mm, v(-1087.01, -43.26) * mm, v(-1112.84, -43.26) * mm, v(-1136.2, -43.26) * mm, v(-1151.88, -43.26) * mm, v(-1165.08, -43.26) * mm, v(-1173.51, -43.26) * mm, v(-1178.4, -43.26) * mm, v(-1181.05, -43.26) * mm, v(-1182.65, -43.26) * mm, v(-1183.5, -43.26) * mm, v(-1182.33, -43.26) * mm, v(-1177.99, -43.26) * mm, v(-1171.32, -43.26) * mm, v(-1162.96, -43.26) * mm, v(-1155.1, -43.26) * mm, v(-1148.57, -43.26) * mm, v(-1143.63, -43.26) * mm, v(-1138.74, -43.26) * mm, v(-1133.95, -43.26) * mm, v(-1129.25, -43.26) * mm, v(-1123.1, -43.26) * mm, v(-1115.6, -43.26) * mm, v(-1103.94, -43.26) * mm, v(-1092.64, -43.26) * mm, v(-1081.48, -43.26) * mm, v(-1073.11, -43.26) * mm, v(-1064.64, -43.26) * mm, v(-1055.9, -43.26) * mm, v(-1046.79, -43.26) * mm, v(-1037.14, -43.26) * mm, v(-1028.55, -43.26) * mm, v(-1021.28, -43.26) * mm, v(-1015.6, -43.26) * mm, v(-1009.73, -43.26) * mm, v(-1001.71, -43.26) * mm, v(-991.47, -43.26) * mm, v(-979.23, -43.26) * mm, v(-967.42, -43.26) * mm, v(-956.46, -43.26) * mm, v(-948.37, -43.26) * mm, v(-942.71, -43.26) * mm, v(-938.93, -43.26) * mm, v(-935.67, -43.26) * mm, v(-932.92, -43.26) * mm, v(-930.58, -43.26) * mm, v(-927.9, -43.26) * mm, v(-925.15, -43.26) * mm, v(-922.18, -43.26) * mm, v(-918.84, -43.26) * mm, v(-914.55, -43.26) * mm, v(-906.9, -43.26) * mm, v(-898.23, -43.26) * mm, v(-890.47, -43.26) * mm, v(-890.47, -43.26) * mm]});
            skLineSegment(sketch, "E186", {"start": v(-799.54, 0) * mm, "end": v(-568.33, 0) * mm});
            skLineSegment(sketch, "E187", {"start": v(-546.97, -12) * mm, "end": v(-799.54, -12) * mm});
            skLineSegment(sketch, "E188", {"start": v(-799.54, -12) * mm, "end": v(-799.54, 0) * mm});
            skArc(sketch, "E189", {"start": v(-546.97, -12) * mm, "mid": v(-534.73, 34.8) * mm, "end": v(-568.33, 0) * mm});
            skLineSegment(sketch, "E190.0", {"start": v(-514.65, -25) * mm, "end": v(-66.51, -25) * mm});
            skSolve(sketch);
        }
        {
            var Q0;
            Q0=qSketchRegion(id+"F20",true);
            extrude(context, id + "F21", {"entities" : qUnion([Q0]), "operationType" : NewBodyOperationType.REMOVE, "endBound" : BoundingType.SYMMETRIC, "oppositeDirection" : true, "depth" : 200 * mm});
        }
    });
